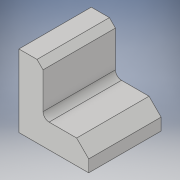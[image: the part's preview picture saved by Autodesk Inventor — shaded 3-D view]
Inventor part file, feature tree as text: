
AUTODESK INVENTOR PART (.ipt)
format: ipt  version: 2018 (Build 220112000, 112)  size: 107,008 bytes
history: native  units: in
note: dims shown in document units (in); Inventor stores cm internally (conversion verified against a paired STEP export)
features: chamfer x2, extrude x1, fillet x1, sketch x1
ambient origin geometry x8: Origin, YZ Plane, XZ Plane, XY Plane, X Axis, Y Axis, Z Axis, Center Point
bodies: Solid1 (feature_tree)
feature tree (5):
  extrude  "Extrusion1"  Depth=0.5in
  chamfer  "Chamfer1"  Distance=1.0in
  chamfer  "Chamfer2"  Distance=1.5in
  fillet  "Fillet2"  Radius=0.125in
  sketch  "Sketch1"  dims[d0=1.5in d1=0.5in d2=1.0in d3=1.5in d4=0.0in d6=0.125in d7=0.125in d8=45.0deg d9=0.25in d10=0.125in d11=45.0deg d12=0.125in]
